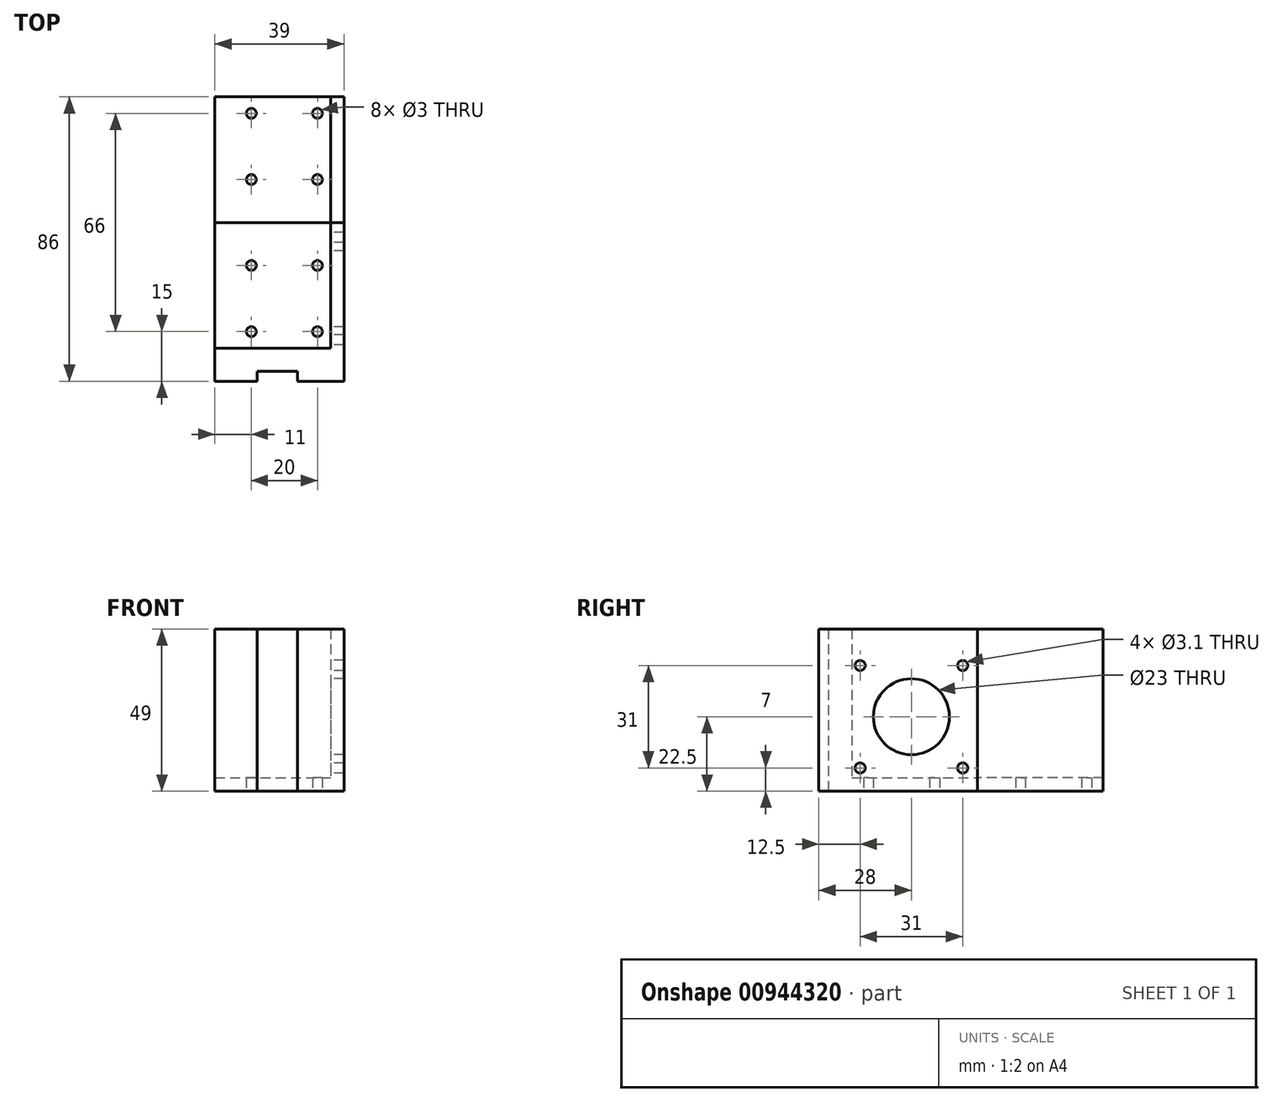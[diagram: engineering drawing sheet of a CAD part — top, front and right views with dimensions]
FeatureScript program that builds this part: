
annotation { "Feature Type Name" : "Feature", "Feature Type Description" : "" }
export const myFeature = defineFeature(function(context is Context, id is Id, definition is map)
    precondition{}
    {
        {
            var Q0;
            Q0=qCreatedBy(makeId("Front.planeOp"),FACE);
            var sketch = newSketch(context, id + "F0", { "sketchPlane" : qUnion([Q0])});
            skLineSegment(sketch, "E0.bottom", {"start": v(0, 0) * mm, "end": v(39, 0) * mm});
            skLineSegment(sketch, "E0.right", {"start": v(39, 0) * mm, "end": v(39, 25) * mm});
            skLineSegment(sketch, "E1.top", {"start": v(0, 4) * mm, "end": v(35, 4) * mm});
            skLineSegment(sketch, "E1.right", {"start": v(35, 23) * mm, "end": v(35, 4) * mm});
            skLineSegment(sketch, "E2", {"start": v(39, 25) * mm, "end": v(39, 49) * mm});
            skLineSegment(sketch, "E3", {"start": v(39, 49) * mm, "end": v(35, 49) * mm});
            skLineSegment(sketch, "E4", {"start": v(35, 49) * mm, "end": v(35, 23) * mm});
            skLineSegment(sketch, "E5", {"start": v(0, 0) * mm, "end": v(0, 4) * mm});
            skSolve(sketch);
        }
        {
            var Q0;
            Q0=makeQuery(id+"F0.imprint","IMPRINT",FACE,{"disambiguationData":[TD([[makeQuery(id+"F0.imprint","IMPRINT",EDGE,{"derivedFrom":sQuery(id+"F0.wireOp",EDGE,"E0.bottom")}),1.0]])]});
            extrude(context, id + "F1", {"entities" : qUnion([Q0]), "depth" : 38 * mm, "offsetDistance" : 25 * mm});
        }
        {
            var Q0;
            Q0=makeQuery(id+"F1.opExtrude","SWEPT_FACE",FACE,{"disambiguationData":[OSD([sQuery(id+"F0.wireOp",EDGE,"E0.bottom")])]});
            var sketch = newSketch(context, id + "F2", { "sketchPlane" : qUnion([Q0])});
            skLineSegment(sketch, "E6", {"start": v(21, 0) * mm, "end": v(21, 38) * mm, "construction": true});
            skLineSegment(sketch, "E7", {"start": v(0, 23) * mm, "end": v(39, 23) * mm, "construction": true});
            skLineSegment(sketch, "E8", {"start": v(39, 23) * mm, "end": v(38.2, 23.72) * mm, "construction": true});
            skCircle(sketch, "E9", {"center": v(11, 13) * mm, "radius": 1.5 * mm});
            skCircle(sketch, "E10.MirrorC", {"center": v(31, 13) * mm, "radius": 1.5 * mm});
            skCircle(sketch, "E11.MirrorC", {"center": v(11, 33) * mm, "radius": 1.5 * mm});
            skCircle(sketch, "E12.MirrorC", {"center": v(31, 33) * mm, "radius": 1.5 * mm});
            skSolve(sketch);
        }
        {
            var Q0;
            Q0=qSketchRegion(id+"F2",true);
            extrude(context, id + "F3", {"entities" : qUnion([Q0]), "operationType" : NewBodyOperationType.REMOVE, "oppositeDirection" : true, "depth" : 25 * mm, "offsetDistance" : 25 * mm});
        }
        {
            var Q0;
            Q0=makeQuery(id+"F1.opExtrude","SWEPT_FACE",FACE,{"disambiguationData":[OSD([sQuery(id+"F0.wireOp",EDGE,"E1.right"),sQuery(id+"F0.wireOp",EDGE,"E4")])]});
            var sketch = newSketch(context, id + "F4", { "sketchPlane" : qUnion([Q0])});
            skLineSegment(sketch, "E13", {"start": v(20, 42.5) * mm, "end": v(20, -7.5) * mm, "construction": true});
            skLineSegment(sketch, "E14", {"start": v(1, 22.5) * mm, "end": v(39, 22.5) * mm, "construction": true});
            skCircle(sketch, "E15", {"center": v(4.5, 38) * mm, "radius": 1.55 * mm});
            skCircle(sketch, "E16.MirrorC", {"center": v(35.5, 38) * mm, "radius": 1.55 * mm});
            skCircle(sketch, "E17.MirrorC", {"center": v(4.5, 7) * mm, "radius": 1.55 * mm});
            skCircle(sketch, "E18.MirrorC", {"center": v(35.5, 7) * mm, "radius": 1.55 * mm});
            skCircle(sketch, "E19", {"center": v(20, 22.5) * mm, "radius": 11.5 * mm});
            skSolve(sketch);
        }
        {
            var Q0;
            Q0=makeQuery(id+"F1.opExtrude","SWEPT_BODY",BODY,{"disambiguationData":[OSD([sQuery(id+"F0.wireOp",EDGE,"E0.bottom"),sQuery(id+"F0.wireOp",EDGE,"E0.right"),sQuery(id+"F0.wireOp",EDGE,"E1.top"),sQuery(id+"F0.wireOp",EDGE,"E1.right"),sQuery(id+"F0.wireOp",EDGE,"E2"),sQuery(id+"F0.wireOp",EDGE,"E3"),sQuery(id+"F0.wireOp",EDGE,"E4"),sQuery(id+"F0.wireOp",EDGE,"E5")])]});
            var Q1;
            Q1=qCreatedBy(makeId("Front.planeOp"),FACE);
            mirror(context, id + "F5", {"entities" : qUnion([Q0]), "mirrorPlane" : qUnion([Q1])});
        }
        {
            var Q0;
            Q0 = qSketchRegion(id + "F4", true);
            extrude(context, id + "F6", {"entities" : qUnion([Q0]), "operationType" : NewBodyOperationType.REMOVE, "endBound" : BoundingType.THROUGH_ALL, "oppositeDirection" : true, "depth" : 25 * mm, "offsetDistance" : 25 * mm});
        }
        {
            var Q0;
            Q0=makeQuery(id+"F1.opExtrude","CAP_FACE",FACE,{"disambiguationData":[OSD([sQuery(id+"F0.wireOp",EDGE,"E0.bottom"),sQuery(id+"F0.wireOp",EDGE,"E0.right"),sQuery(id+"F0.wireOp",EDGE,"E1.top"),sQuery(id+"F0.wireOp",EDGE,"E1.right"),sQuery(id+"F0.wireOp",EDGE,"E2"),sQuery(id+"F0.wireOp",EDGE,"E3"),sQuery(id+"F0.wireOp",EDGE,"E4"),sQuery(id+"F0.wireOp",EDGE,"E5")])],"isStart":false});
            var sketch = newSketch(context, id + "F7", { "sketchPlane" : qUnion([Q0])});
            skLineSegment(sketch, "E20.bottom", {"start": v(39, 0) * mm, "end": v(0, 0) * mm});
            skLineSegment(sketch, "E20.top", {"start": v(39, 49) * mm, "end": v(0, 49) * mm});
            skLineSegment(sketch, "E20.left", {"start": v(39, 0) * mm, "end": v(39, 49) * mm});
            skLineSegment(sketch, "E20.right", {"start": v(0, 0) * mm, "end": v(0, 49) * mm});
            skSolve(sketch);
        }
        {
            var Q0;
            Q0 = qSketchRegion(id + "F7", true);
            extrude(context, id + "F8", {"entities" : qUnion([Q0]), "operationType" : NewBodyOperationType.ADD, "depth" : 10 * mm, "offsetDistance" : 25 * mm});
        }
        {
            var Q0;
            Q0=makeQuery(id+"F8.boolean.opBoolean","MERGE",FACE,{"derivedFrom":[makeQuery(id+"F1.opExtrude","SWEPT_FACE",FACE,{"disambiguationData":[OSD([sQuery(id+"F0.wireOp",EDGE,"E3")])]}),makeQuery(id+"F8.opExtrude","SWEPT_FACE",FACE,{"disambiguationData":[OSD([sQuery(id+"F7.wireOp",EDGE,"E20.top")])]})]});
            var sketch = newSketch(context, id + "F9", { "sketchPlane" : qUnion([Q0])});
            skLineSegment(sketch, "E21.bottom", {"start": v(12.8, -48) * mm, "end": v(25, -48) * mm});
            skLineSegment(sketch, "E21.top", {"start": v(12.8, -45) * mm, "end": v(25, -45) * mm});
            skLineSegment(sketch, "E21.left", {"start": v(12.8, -48) * mm, "end": v(12.8, -45) * mm});
            skLineSegment(sketch, "E21.right", {"start": v(25, -48) * mm, "end": v(25, -45) * mm});
            skSolve(sketch);
        }
        {
            var Q0;
            Q0 = qSketchRegion(id + "F9", true);
            extrude(context, id + "F10", {"entities" : qUnion([Q0]), "operationType" : NewBodyOperationType.REMOVE, "endBound" : BoundingType.THROUGH_ALL, "oppositeDirection" : true, "depth" : 25 * mm, "offsetDistance" : 25 * mm});
        }
    });
